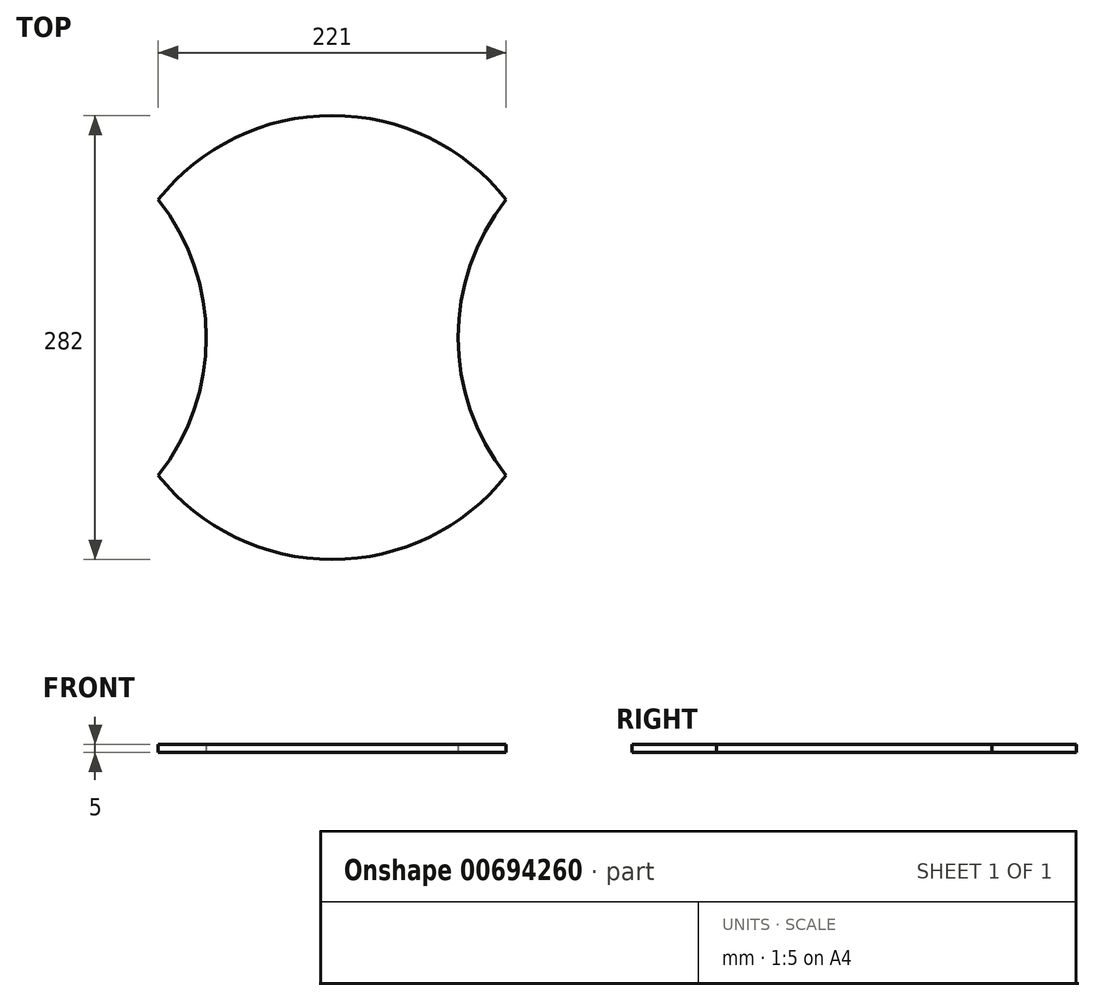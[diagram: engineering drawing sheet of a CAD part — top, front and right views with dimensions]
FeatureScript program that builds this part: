
annotation { "Feature Type Name" : "Feature", "Feature Type Description" : "" }
export const myFeature = defineFeature(function(context is Context, id is Id, definition is map)
    precondition{}
    {
        {
            var Q0;
            Q0=qCreatedBy(makeId("Top.planeOp"),FACE);
            var sketch = newSketch(context, id + "F0", { "sketchPlane" : qUnion([Q0])});
            skArc(sketch, "E0", {"start": v(-110.5, -87.58) * mm, "mid": v(0, -141) * mm, "end": v(110.5, -87.58) * mm});
            skArc(sketch, "E1", {"start": v(-110.5, -87.58) * mm, "mid": v(-80, 0) * mm, "end": v(-110.5, 87.58) * mm});
            skArc(sketch, "E2", {"start": v(110.5, 87.58) * mm, "mid": v(80, 0) * mm, "end": v(110.5, -87.58) * mm});
            skArc(sketch, "E3.trimOffspring", {"start": v(110.5, 87.58) * mm, "mid": v(0, 141) * mm, "end": v(-110.5, 87.58) * mm});
            skSolve(sketch);
        }
        {
            var Q0;
            Q0=makeQuery(id+"F0.imprint","IMPRINT",FACE,{"disambiguationData":[TD([[makeQuery(id+"F0.imprint","IMPRINT",EDGE,{"derivedFrom":sQuery(id+"F0.wireOp",EDGE,"E0")}),1.0]])]});
            extrude(context, id + "F1", {"entities" : qUnion([Q0]), "depth" : 2.5 * mm, "offsetDistance" : 25 * mm, "hasSecondDirection" : true, "secondDirectionOppositeDirection" : true, "secondDirectionDepth" : 2.5 * mm});
        }
    });
